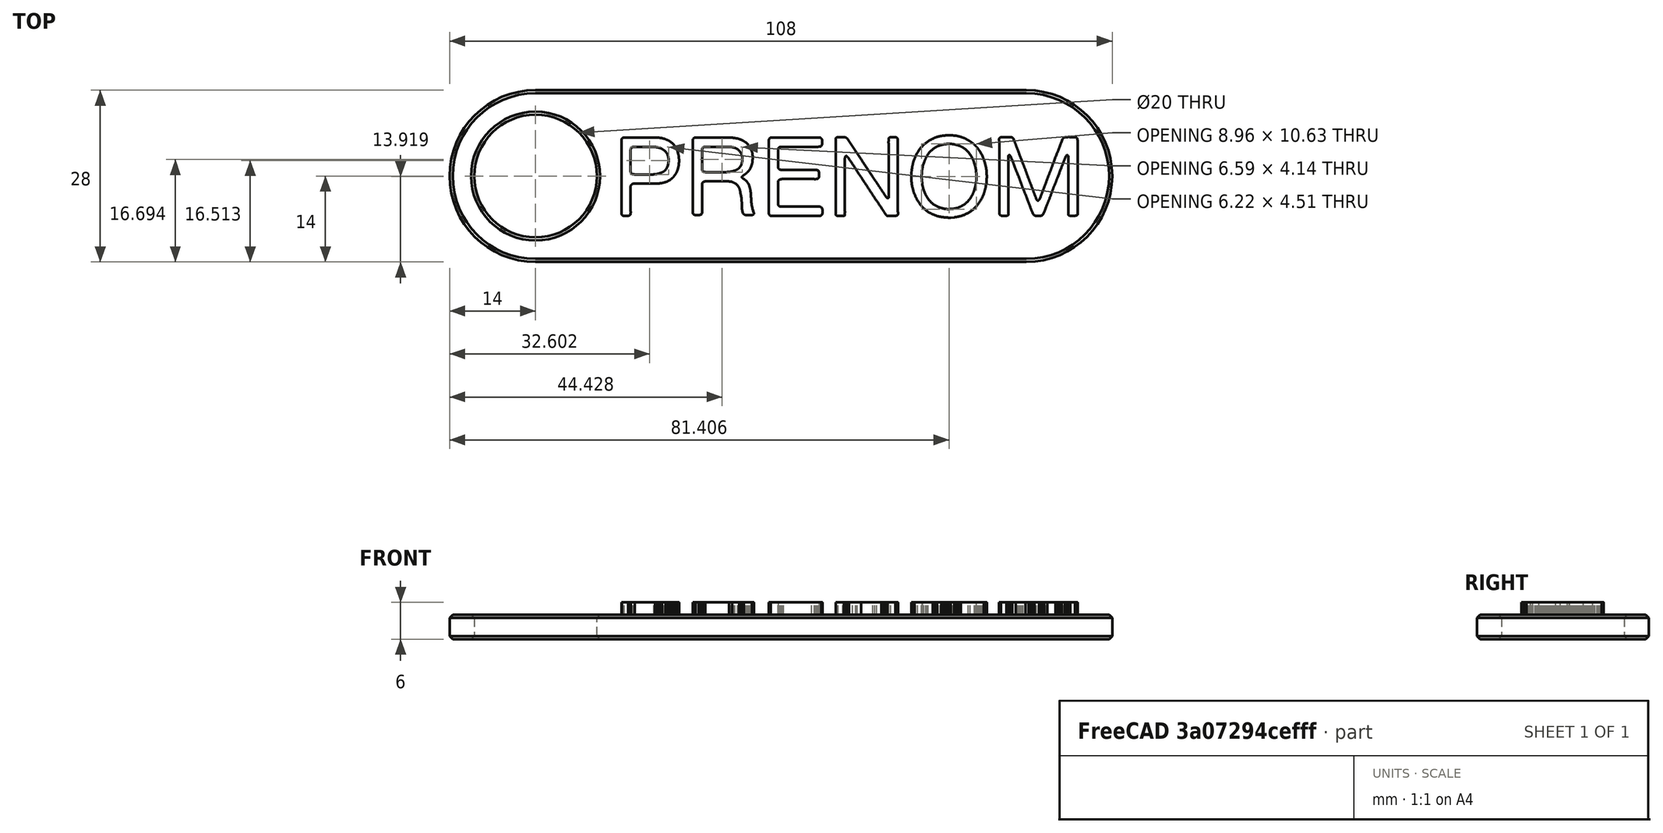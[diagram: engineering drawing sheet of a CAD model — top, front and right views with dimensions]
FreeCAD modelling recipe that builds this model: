
FCSTD DOCUMENT  (FreeCAD 0.16R6706 (Git))
Label: simple_nametag
License: All rights reserved
LicenseURL: http://en.wikipedia.org/wiki/All_rights_reserved
objects: PartDesign::Pad×2, Sketcher::SketchObject×1, PartDesign::Chamfer×1, Part::Part2DObjectPython×1
note: 7 computed .brp shape members not serialized (recipe doc carries the construction recipe); baked Part::Feature solids carry a one-line shape summary decoded from their .brp

FEATURE [Sketcher::SketchObject] Sketch
  sketch-geometry (5):
    g0: Circle CenterX=0 CenterY=0 CenterZ=0 NormalX=0 NormalY=0 NormalZ=1 Radius=10
    g1: ArcOfCircle CenterX=0 CenterY=0 CenterZ=0 NormalX=0 NormalY=0 NormalZ=1 Radius=14 StartAngle=1.5708 EndAngle=4.71239
    g2: ArcOfCircle CenterX=80 CenterY=0 CenterZ=0 NormalX=0 NormalY=0 NormalZ=1 Radius=14 StartAngle=4.71239 EndAngle=7.85398
    g3: LineSegment StartX=0 StartY=-14 StartZ=0 EndX=80 EndY=-14 EndZ=0
    g4: LineSegment StartX=0 StartY=14 StartZ=0 EndX=80 EndY=14 EndZ=0
  constraints (11):
    c: Tangent(g1,g4) = 1.5708
    c: Tangent(g1,g3) = -1.5708
    c: Tangent(g3,g2) = -1.5708
    c: Tangent(g4,g2) = 1.5708
    c: Horizontal(g3)
    c: Equal(g1,g2)
    c: Coincident(g0,g-1)
    c: Coincident(g1,g-1)
    c: Radius(g0) = 10
    c: Radius(g1) = 14
    c: DistanceX(g4,g4) = 80
FEATURE [PartDesign::Pad] Pad
  Length = 4
  Length2 = 100
  Sketch = -> Sketch
  Type = 0
FEATURE [PartDesign::Chamfer] Chamfer
  Base = -> Pad [Edge4,Edge7,Edge10,Edge12,Edge15,Edge3,Edge6,Edge9,Edge11,Edge14]
  Size = 0.5
FEATURE [Part::Part2DObjectPython] ShapeString  # Draft 2D object (typed FeaturePython)
  FontFile = <path> ARTS/FONTS/Fonts/AlteHaasGroteskRegular.ttf
  Placement = pos=(12.5,-6.5,4) rot=(0,0,1;0rad)
  Size = 7
  String = PRENOM
  Tracking = 0
FEATURE [PartDesign::Pad] Pad001
  Length = 2
  Length2 = 100
  Placement = pos=(12.5,-6.5,4) rot=(0,0,1;0rad)
  Sketch = -> ShapeString
  Type = 0
note: 1 file-system path scrubbed to <path> (originals preserved in the JSON sidecar)
